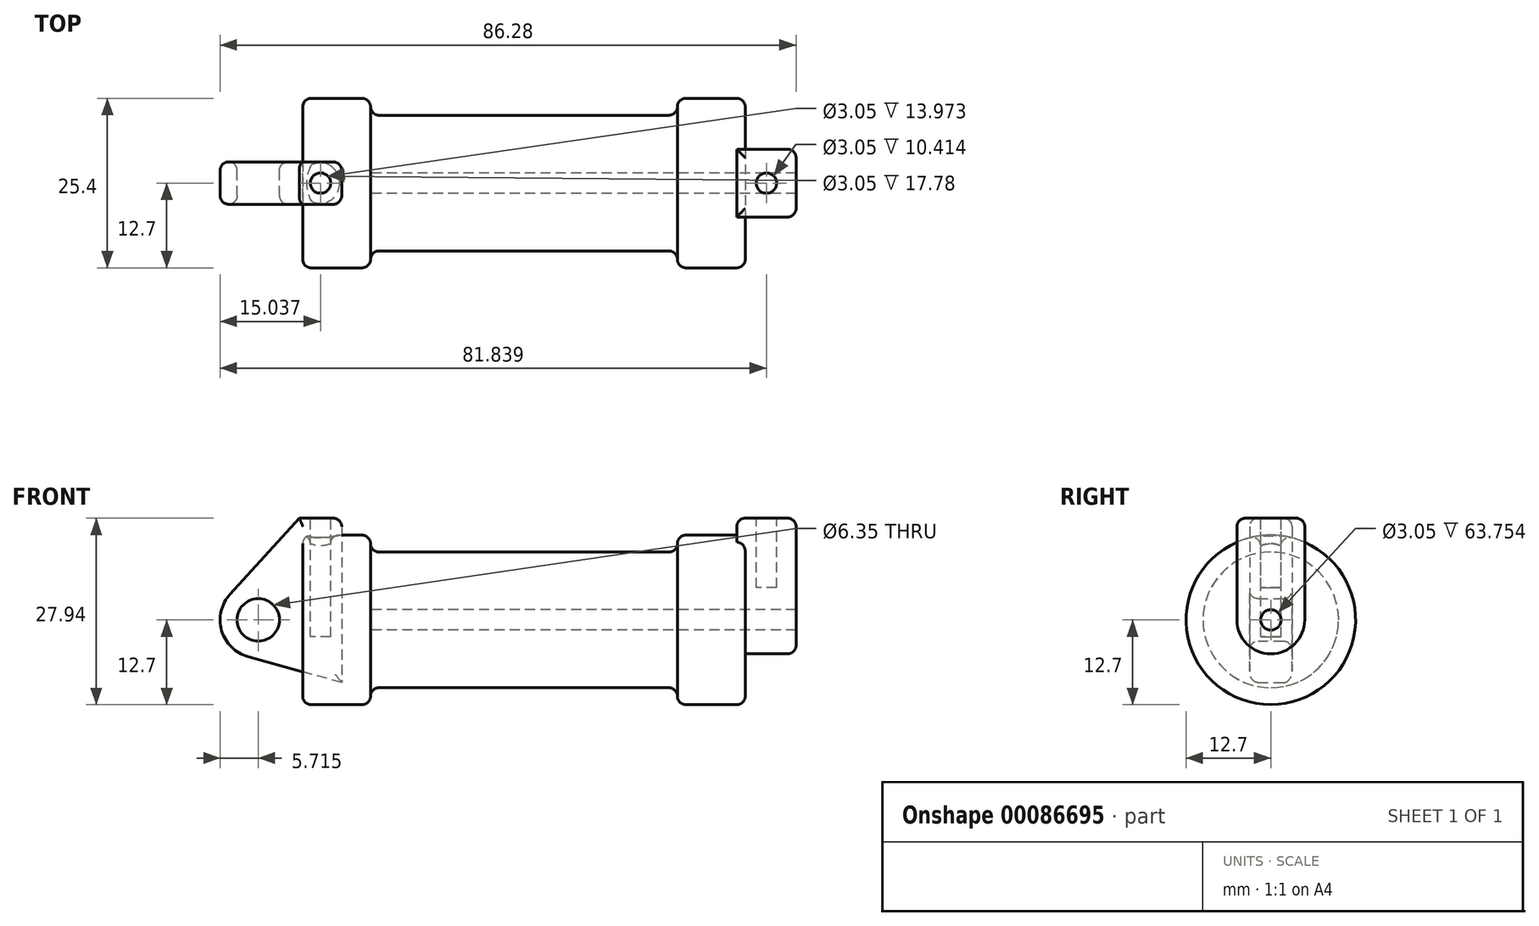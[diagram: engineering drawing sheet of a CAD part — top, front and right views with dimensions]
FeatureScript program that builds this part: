
annotation { "Feature Type Name" : "Feature", "Feature Type Description" : "" }
export const myFeature = defineFeature(function(context is Context, id is Id, definition is map)
    precondition{}
    {
        {
            var Q0;
            Q0=qCreatedBy(makeId("Front.planeOp"),FACE);
            var sketch = newSketch(context, id + "F0", { "sketchPlane" : qUnion([Q0])});
            skLineSegment(sketch, "E0", {"start": v(0, 0) * mm, "end": v(0, 12.7) * mm});
            skLineSegment(sketch, "E1", {"start": v(0, 12.7) * mm, "end": v(10.16, 12.7) * mm});
            skLineSegment(sketch, "E2", {"start": v(10.16, 12.7) * mm, "end": v(10.16, 10.16) * mm});
            skLineSegment(sketch, "E3", {"start": v(10.16, 10.16) * mm, "end": v(56.13, 10.16) * mm});
            skLineSegment(sketch, "E4", {"start": v(56.13, 10.16) * mm, "end": v(56.13, 12.7) * mm});
            skLineSegment(sketch, "E5", {"start": v(56.13, 12.7) * mm, "end": v(66.3, 12.7) * mm});
            skLineSegment(sketch, "E6", {"start": v(66.3, 12.7) * mm, "end": v(66.3, 0) * mm});
            skLineSegment(sketch, "E7", {"start": v(66.3, 0) * mm, "end": v(0, 0) * mm});
            skLineSegment(sketch, "E8", {"start": v(5.84, 15.24) * mm, "end": v(-0.5, 15.24) * mm});
            skLineSegment(sketch, "E9", {"start": v(-0.5, 15.24) * mm, "end": v(-10.88, 3.85) * mm});
            skLineSegment(sketch, "E10", {"start": v(0, 0) * mm, "end": v(-6.65, 0) * mm});
            skCircle(sketch, "E11", {"center": v(-6.65, 0) * mm, "radius": 5.72 * mm});
            skCircle(sketch, "E12", {"center": v(-6.65, 0) * mm, "radius": 3.18 * mm});
            skLineSegment(sketch, "E13", {"start": v(5.84, 15.24) * mm, "end": v(5.84, -9.4) * mm});
            skLineSegment(sketch, "E14", {"start": v(5.84, -9.4) * mm, "end": v(-8.18, -5.5) * mm});
            skSolve(sketch);
        }
        {
            var Q0;
            {var subQ3=sQuery(id+"F0.wireOp",EDGE,"E0");Q0=makeQuery(id+"F0.imprint","IMPRINT",FACE,{"disambiguationData":[TD([[makeQuery(id+"F0.imprint","IMPRINT",EDGE,{"derivedFrom":subQ3}),1.0]])]});}
            var Q1;
            {var subQ0=sQuery(id+"F0.wireOp",EDGE,"E0");Q1=makeQuery(id+"F0.imprint","IMPRINT",FACE,{"disambiguationData":[TD([[makeQuery(id+"F0.imprint","IMPRINT",EDGE,{"derivedFrom":subQ0}),-1.0]])]});}
            var Q2;
            {var subQ0=sQuery(id+"F0.wireOp",EDGE,"E14");Q2=makeQuery(id+"F0.imprint","IMPRINT",FACE,{"disambiguationData":[TD([[makeQuery(id+"F0.imprint","IMPRINT",EDGE,{"derivedFrom":subQ0}),-1.0]])]});}
            var Q3;
            {var subQ4=sQuery(id+"F0.wireOp",EDGE,"E12");Q3=makeQuery(id+"F0.imprint","IMPRINT",FACE,{"disambiguationData":[TD([[makeQuery(id+"F0.imprint","IMPRINT",EDGE,{"derivedFrom":subQ4}),-1.0]])]});}
            extrude(context, id + "F1", {"entities" : qUnion([Q0, Q1, Q2, Q3]), "endBound" : BoundingType.SYMMETRIC, "depth" : 6.35 * mm});
        }
        {
            var Q0;
            {var subQ0=sQuery(id+"F0.wireOp",EDGE,"E2");Q0=makeQuery(id+"F0.imprint","IMPRINT",FACE,{"disambiguationData":[TD([[makeQuery(id+"F0.imprint","IMPRINT",EDGE,{"derivedFrom":subQ0}),-1.0]])]});}
            var Q1;
            {var subQ0=sQuery(id+"F0.wireOp",EDGE,"E0");Q1=makeQuery(id+"F0.imprint","IMPRINT",FACE,{"disambiguationData":[TD([[makeQuery(id+"F0.imprint","IMPRINT",EDGE,{"derivedFrom":subQ0}),-1.0]])]});}
            var Q2;
            Q2=sQuery(id+"F0.wireOp",EDGE,"E7");
            revolve(context, id + "F2", {"entities" : qUnion([Q0, Q1]), "axis" : qUnion([Q2]), "revolveType" : RevolveType.FULL});
        }
        {
            var Q0;
            Q0=makeQuery(id+"F2.opRevolve","SWEPT_FACE",FACE,{"disambiguationData":[OSD([sQuery(id+"F0.wireOp",EDGE,"E6")])]});
            var sketch = newSketch(context, id + "F3", { "sketchPlane" : qUnion([Q0])});
            skCircle(sketch, "E15", {"center": v(0, 0) * mm, "radius": 1.52 * mm});
            skCircle(sketch, "E16", {"center": v(0, 0) * mm, "radius": 5.08 * mm});
            skLineSegment(sketch, "E17", {"start": v(5.08, 0) * mm, "end": v(5.08, 15.24) * mm});
            skLineSegment(sketch, "E18", {"start": v(-5.08, 0) * mm, "end": v(-5.08, 15.24) * mm});
            skLineSegment(sketch, "E19", {"start": v(5.08, 15.24) * mm, "end": v(-5.08, 15.24) * mm});
            skSolve(sketch);
        }
        {
            var Q0;
            {var subQ0=sQuery(id+"F3.wireOp",EDGE,"E17");var subQ1=sQuery(id+"F3.wireOp",EDGE,"E16");var subQ2=makeQuery(id+"F3.imprint","INTERSECT",VERTEX,{"derivedFrom":[subQ1,subQ0]});Q0=makeQuery(id+"F3.imprint","IMPRINT",FACE,{"disambiguationData":[TD([[makeQuery(id+"F3.imprint","IMPRINT",EDGE,{"disambiguationData":[TD([[subQ2,-1.0]])],"derivedFrom":subQ1}),-1.0]])]});}
            var Q1;
            Q1=makeQuery(id+"F3.imprint","IMPRINT",FACE,{"disambiguationData":[TD([[makeQuery(id+"F3.imprint","IMPRINT",EDGE,{"derivedFrom":sQuery(id+"F3.wireOp",EDGE,"E15")}),-1.0]])]});
            var Q2;
            {var subQ0=sQuery(id+"F3.wireOp",EDGE,"E19");Q2=makeQuery(id+"F3.imprint","IMPRINT",FACE,{"disambiguationData":[TD([[makeQuery(id+"F3.imprint","IMPRINT",EDGE,{"derivedFrom":subQ0}),1.0]])]});}
            extrude(context, id + "F4", {"entities" : qUnion([Q0, Q1, Q2]), "operationType" : NewBodyOperationType.ADD, "depth" : 7.62 * mm});
        }
        {
            var Q0;
            Q0=makeQuery(id+"F4.opExtrude","CAP_FACE",FACE,{"disambiguationData":[OSD([sQuery(id+"F3.wireOp",EDGE,"E15"),sQuery(id+"F3.wireOp",EDGE,"E16"),sQuery(id+"F3.wireOp",EDGE,"E17"),sQuery(id+"F3.wireOp",EDGE,"E18"),sQuery(id+"F3.wireOp",EDGE,"E19")])],"isStart":true});
            extrude(context, id + "F5", {"entities" : qUnion([Q0]), "operationType" : NewBodyOperationType.ADD, "depth" : 1.27 * mm});
        }
        {
            var Q0;
            Q0=makeQuery(id+"F4.boolean.opBoolean","SPLIT",FACE,{"disambiguationData":[TD([makeQuery(id+"F4.opExtrude","SWEPT_FACE",FACE,{"disambiguationData":[OSD([sQuery(id+"F3.wireOp",EDGE,"E15")])]})])],"derivedFrom":makeQuery(id+"F2.opRevolve","SWEPT_FACE",FACE,{"disambiguationData":[OSD([sQuery(id+"F0.wireOp",EDGE,"E6")])]})});
            var Q1;
            Q1=makeQuery(id+"F2.opRevolve","SWEPT_FACE",FACE,{"disambiguationData":[OSD([sQuery(id+"F0.wireOp",EDGE,"E2")])]});
            extrude(context, id + "F6", {"entities" : qUnion([Q0]), "operationType" : NewBodyOperationType.REMOVE, "endBound" : BoundingType.UP_TO_SURFACE, "oppositeDirection" : true, "endBoundEntityFace" : qUnion([Q1]), "depth" : 25.4 * mm});
        }
        {
            var Q0;
            Q0=makeQuery(id+"F1.opExtrude","SWEPT_FACE",FACE,{"disambiguationData":[OSD([sQuery(id+"F0.wireOp",EDGE,"E8")])]});
            var sketch = newSketch(context, id + "F7", { "sketchPlane" : qUnion([Q0])});
            skLineSegment(sketch, "E20", {"start": v(2.67, 3.18) * mm, "end": v(2.67, -3.18) * mm, "construction": true});
            skCircle(sketch, "E21", {"center": v(2.67, 0) * mm, "radius": 1.52 * mm});
            skSolve(sketch);
        }
        {
            var Q0;
            Q0=makeQuery(id+"F7.imprint","IMPRINT",FACE,{"disambiguationData":[TD([[makeQuery(id+"F7.imprint","IMPRINT",EDGE,{"derivedFrom":sQuery(id+"F7.wireOp",EDGE,"E21")}),1.0]])]});
            extrude(context, id + "F8", {"entities" : qUnion([Q0]), "operationType" : NewBodyOperationType.REMOVE, "oppositeDirection" : true, "depth" : 17.78 * mm});
        }
        {
            var Q0;
            {var subQ0=sQuery(id+"F3.wireOp",EDGE,"E19");Q0=makeQuery(id+"F5.boolean.opBoolean","MERGE",FACE,{"derivedFrom":[makeQuery(id+"F4.opExtrude","SWEPT_FACE",FACE,{"disambiguationData":[OSD([subQ0])]}),makeQuery(id+"F5.opExtrude","SWEPT_FACE",FACE,{"disambiguationData":[OSD([subQ0])]})]});}
            var sketch = newSketch(context, id + "F9", { "sketchPlane" : qUnion([Q0])});
            skLineSegment(sketch, "E22", {"start": v(69.47, 5.08) * mm, "end": v(69.47, -5.08) * mm, "construction": true});
            skCircle(sketch, "E23", {"center": v(69.47, 0) * mm, "radius": 1.52 * mm});
            skSolve(sketch);
        }
        {
            var Q0;
            Q0=makeQuery(id+"F9.imprint","IMPRINT",FACE,{"disambiguationData":[TD([[makeQuery(id+"F9.imprint","IMPRINT",EDGE,{"derivedFrom":sQuery(id+"F9.wireOp",EDGE,"E23")}),1.0]])]});
            extrude(context, id + "F10", {"entities" : qUnion([Q0]), "operationType" : NewBodyOperationType.REMOVE, "oppositeDirection" : true, "depth" : 10.4 * mm});
        }
        {
            var Q0;
            Q0=makeQuery(id+"F2.opRevolve","SWEPT_FACE",FACE,{"disambiguationData":[OSD([sQuery(id+"F0.wireOp",EDGE,"E3")])]});
            var Q1;
            Q1=makeQuery(id+"F2.opRevolve","SWEPT_FACE",FACE,{"disambiguationData":[OSD([sQuery(id+"F0.wireOp",EDGE,"E1")])]});
            var Q2;
            Q2=makeQuery(id+"F1.opExtrude","CAP_FACE",FACE,{"disambiguationData":[OSD([sQuery(id+"F0.wireOp",EDGE,"E8"),sQuery(id+"F0.wireOp",EDGE,"E9"),sQuery(id+"F0.wireOp",EDGE,"E11"),sQuery(id+"F0.wireOp",EDGE,"E12"),sQuery(id+"F0.wireOp",EDGE,"E13"),sQuery(id+"F0.wireOp",EDGE,"E14")])],"isStart":false});
            var Q3;
            Q3=makeQuery(id+"F1.opExtrude","CAP_FACE",FACE,{"disambiguationData":[OSD([sQuery(id+"F0.wireOp",EDGE,"E8"),sQuery(id+"F0.wireOp",EDGE,"E9"),sQuery(id+"F0.wireOp",EDGE,"E11"),sQuery(id+"F0.wireOp",EDGE,"E12"),sQuery(id+"F0.wireOp",EDGE,"E13"),sQuery(id+"F0.wireOp",EDGE,"E14")])],"isStart":true});
            var Q4;
            Q4=makeQuery(id+"F1.opExtrude","CAP_EDGE",EDGE,{"disambiguationData":[OSD([sQuery(id+"F0.wireOp",EDGE,"E8")])],"isStart":false});
            var Q5;
            Q5=makeQuery(id+"F1.opExtrude","SWEPT_EDGE",EDGE,{"disambiguationData":[OSD([sQuery(id+"F0.wireOp",EDGE,"E8"),sQuery(id+"F0.wireOp",EDGE,"E13")])]});
            var Q6;
            Q6=makeQuery(id+"F1.opExtrude","CAP_EDGE",EDGE,{"disambiguationData":[OSD([sQuery(id+"F0.wireOp",EDGE,"E8")])],"isStart":true});
            var Q7;
            Q7=makeQuery(id+"F1.opExtrude","CAP_EDGE",EDGE,{"disambiguationData":[OSD([sQuery(id+"F0.wireOp",EDGE,"E9")])],"isStart":true});
            var Q8;
            Q8=makeQuery(id+"F4.boolean.opBoolean","SPLIT",EDGE,{"disambiguationData":[OD(1.0)],"derivedFrom":makeQuery(id+"F2.opRevolve","SWEPT_EDGE",EDGE,{"disambiguationData":[OSD([sQuery(id+"F0.wireOp",EDGE,"E5"),sQuery(id+"F0.wireOp",EDGE,"E6")])]})});
            var Q9;
            Q9=makeQuery(id+"F2.opRevolve","SWEPT_EDGE",EDGE,{"disambiguationData":[OSD([sQuery(id+"F0.wireOp",EDGE,"E4"),sQuery(id+"F0.wireOp",EDGE,"E5")])]});
            var Q10;
            Q10=makeQuery(id+"F4.opExtrude","CAP_EDGE",EDGE,{"disambiguationData":[OSD([sQuery(id+"F3.wireOp",EDGE,"E16")])],"isStart":false});
            var Q11;
            Q11=makeQuery(id+"F4.opExtrude","CAP_EDGE",EDGE,{"disambiguationData":[OSD([sQuery(id+"F3.wireOp",EDGE,"E17")])],"isStart":false});
            var Q12;
            Q12=makeQuery(id+"F4.opExtrude","CAP_EDGE",EDGE,{"disambiguationData":[OSD([sQuery(id+"F3.wireOp",EDGE,"E18")])],"isStart":false});
            var Q13;
            {var subQ0=sQuery(id+"F3.wireOp",EDGE,"E19");var subQ1=sQuery(id+"F3.wireOp",EDGE,"E17");Q13=makeQuery(id+"F5.boolean.opBoolean","MERGE",EDGE,{"derivedFrom":[makeQuery(id+"F4.opExtrude","SWEPT_EDGE",EDGE,{"disambiguationData":[OSD([subQ1,subQ0])]}),makeQuery(id+"F5.opExtrude","SWEPT_EDGE",EDGE,{"disambiguationData":[OSD([subQ1,subQ0])]})]});}
            var Q14;
            Q14=makeQuery(id+"F4.opExtrude","CAP_EDGE",EDGE,{"disambiguationData":[OSD([sQuery(id+"F3.wireOp",EDGE,"E19")])],"isStart":false});
            var Q15;
            Q15=makeQuery(id+"F5.opExtrude","CAP_EDGE",EDGE,{"disambiguationData":[OSD([sQuery(id+"F3.wireOp",EDGE,"E19")])],"isStart":false});
            var Q16;
            {var subQ0=sQuery(id+"F3.wireOp",EDGE,"E19");var subQ1=sQuery(id+"F3.wireOp",EDGE,"E18");Q16=makeQuery(id+"F5.boolean.opBoolean","MERGE",EDGE,{"derivedFrom":[makeQuery(id+"F4.opExtrude","SWEPT_EDGE",EDGE,{"disambiguationData":[OSD([subQ1,subQ0])]}),makeQuery(id+"F5.opExtrude","SWEPT_EDGE",EDGE,{"disambiguationData":[OSD([subQ1,subQ0])]})]});}
            fillet(context, id + "F11", {"entities" : qUnion([Q0, Q1, Q2, Q3, Q4, Q5, Q6, Q7, Q8, Q9, Q10, Q11, Q12, Q13, Q14, Q15, Q16]), "radius" : 1.27 * mm, "allowEdgeOverflow" : false});
        }
    });
